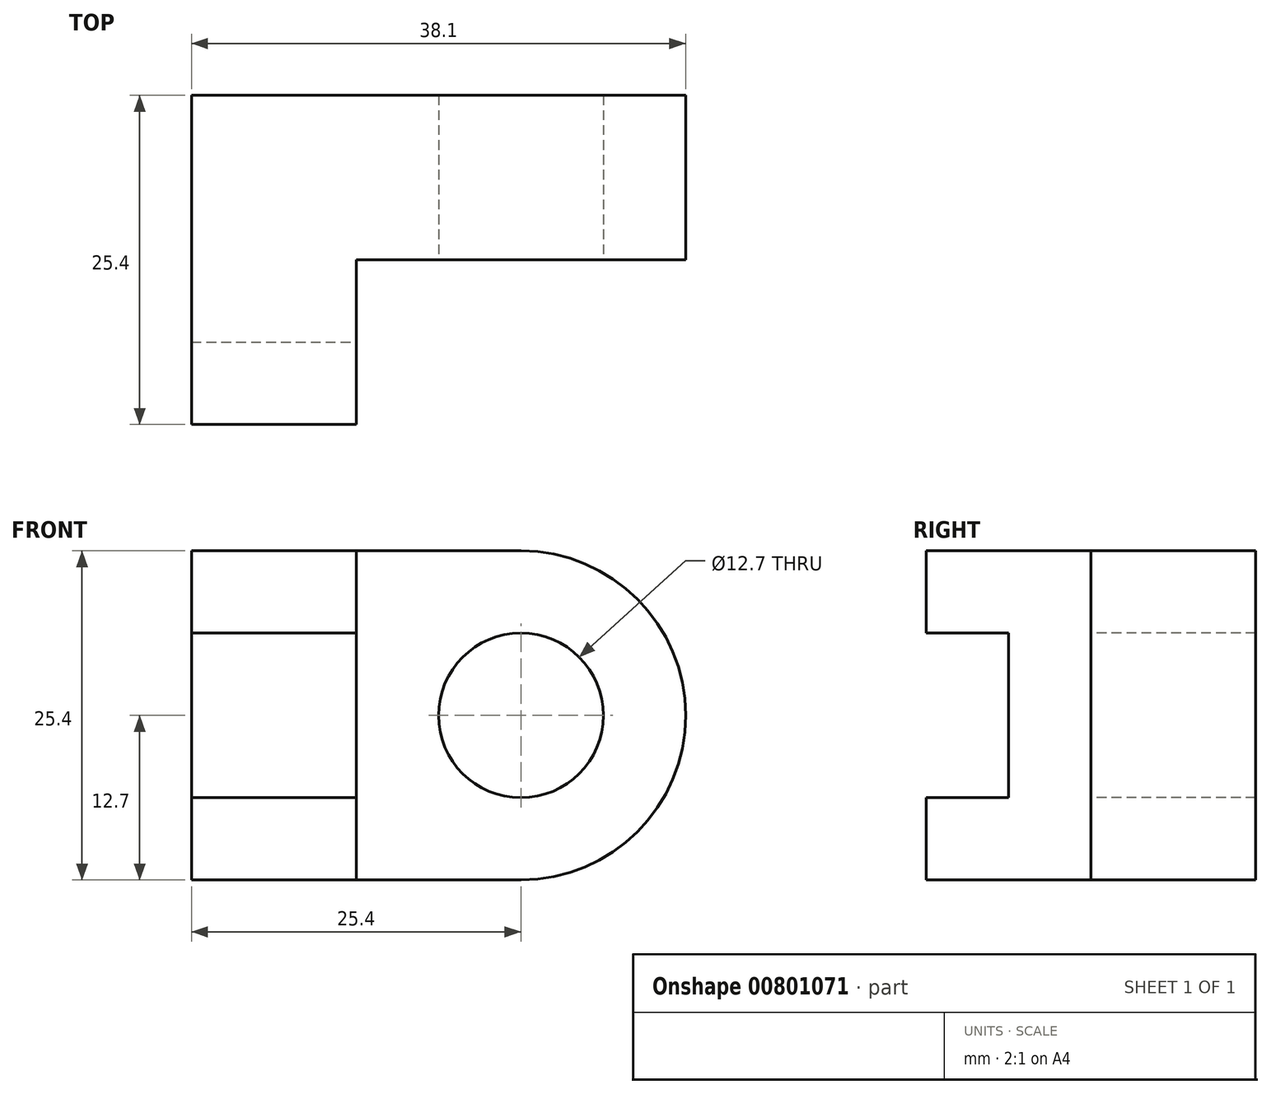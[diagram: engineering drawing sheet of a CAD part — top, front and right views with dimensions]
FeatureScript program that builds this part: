
annotation { "Feature Type Name" : "Feature", "Feature Type Description" : "" }
export const myFeature = defineFeature(function(context is Context, id is Id, definition is map)
    precondition{}
    {
        {
            var Q0;
            Q0=qCreatedBy(makeId("Front.planeOp"),FACE);
            var sketch = newSketch(context, id + "F0", { "sketchPlane" : qUnion([Q0])});
            skLineSegment(sketch, "E0", {"start": v(0, 0) * mm, "end": v(44.45, 0) * mm});
            skLineSegment(sketch, "E1", {"start": v(0, 0) * mm, "end": v(0, 25.4) * mm});
            skLineSegment(sketch, "E2", {"start": v(0, 25.4) * mm, "end": v(44.45, 25.4) * mm});
            skLineSegment(sketch, "E3", {"start": v(44.45, 25.4) * mm, "end": v(44.45, 0) * mm});
            skSolve(sketch);
        }
        {
            var Q0;
            Q0=makeQuery(id+"F0.imprint","IMPRINT",FACE,{"disambiguationData":[TD([[makeQuery(id+"F0.imprint","IMPRINT",EDGE,{"derivedFrom":sQuery(id+"F0.wireOp",EDGE,"E0")}),1.0]])]});
            extrude(context, id + "F1", {"entities" : qUnion([Q0]), "depth" : 25.4 * mm, "offsetDistance" : 25.4 * mm});
        }
        {
            var Q0;
            Q0=makeQuery(id+"F1.opExtrude","CAP_FACE",FACE,{"disambiguationData":[OSD([sQuery(id+"F0.wireOp",EDGE,"E0"),sQuery(id+"F0.wireOp",EDGE,"E1"),sQuery(id+"F0.wireOp",EDGE,"E2"),sQuery(id+"F0.wireOp",EDGE,"E3")])],"isStart":false});
            var sketch = newSketch(context, id + "F2", { "sketchPlane" : qUnion([Q0])});
            skLineSegment(sketch, "E4", {"start": v(0, 25.4) * mm, "end": v(0, 19.05) * mm, "construction": true});
            skLineSegment(sketch, "E5", {"start": v(0, 0) * mm, "end": v(0, 6.35) * mm, "construction": true});
            skLineSegment(sketch, "E6", {"start": v(0, 25.4) * mm, "end": v(12.7, 25.4) * mm, "construction": true});
            skLineSegment(sketch, "E7", {"start": v(12.7, 25.4) * mm, "end": v(12.7, 0) * mm, "construction": true});
            skLineSegment(sketch, "E8", {"start": v(0, 19.05) * mm, "end": v(12.7, 19.05) * mm});
            skLineSegment(sketch, "E9", {"start": v(12.7, 19.05) * mm, "end": v(12.7, 6.35) * mm});
            skLineSegment(sketch, "E10", {"start": v(12.7, 6.35) * mm, "end": v(0, 6.35) * mm});
            skLineSegment(sketch, "E11", {"start": v(0, 6.35) * mm, "end": v(0, 19.05) * mm});
            skSolve(sketch);
        }
        {
            var Q0;
            Q0=makeQuery(id+"F2.imprint","IMPRINT",FACE,{"disambiguationData":[TD([[makeQuery(id+"F2.imprint","IMPRINT",EDGE,{"derivedFrom":sQuery(id+"F2.wireOp",EDGE,"E8")}),-1.0]])]});
            extrude(context, id + "F3", {"entities" : qUnion([Q0]), "operationType" : NewBodyOperationType.REMOVE, "oppositeDirection" : true, "depth" : 6.35 * mm, "offsetDistance" : 25.4 * mm});
        }
        {
            var Q0;
            Q0=makeQuery(id+"F1.opExtrude","SWEPT_FACE",FACE,{"disambiguationData":[OSD([sQuery(id+"F0.wireOp",EDGE,"E2")])]});
            var sketch = newSketch(context, id + "F4", { "sketchPlane" : qUnion([Q0])});
            skLineSegment(sketch, "E12", {"start": v(0, -25.4) * mm, "end": v(12.7, -25.4) * mm, "construction": true});
            skLineSegment(sketch, "E13", {"start": v(12.7, -25.4) * mm, "end": v(12.7, -12.7) * mm, "construction": true});
            skLineSegment(sketch, "E14", {"start": v(12.7, -25.4) * mm, "end": v(12.7, -12.7) * mm});
            skLineSegment(sketch, "E15", {"start": v(12.7, -12.7) * mm, "end": v(44.45, -12.7) * mm});
            skLineSegment(sketch, "E16", {"start": v(44.45, -12.7) * mm, "end": v(44.45, -25.4) * mm});
            skLineSegment(sketch, "E17", {"start": v(44.45, -25.4) * mm, "end": v(12.7, -25.4) * mm});
            skSolve(sketch);
        }
        {
            var Q0;
            Q0=makeQuery(id+"F4.imprint","IMPRINT",FACE,{"disambiguationData":[TD([[makeQuery(id+"F4.imprint","IMPRINT",EDGE,{"derivedFrom":sQuery(id+"F4.wireOp",EDGE,"E14")}),-1.0]])]});
            extrude(context, id + "F5", {"entities" : qUnion([Q0]), "operationType" : NewBodyOperationType.REMOVE, "oppositeDirection" : true, "depth" : 25.4 * mm, "offsetDistance" : 25.4 * mm});
        }
        {
            var Q0;
            Q0=makeQuery(id+"F5.boolean.opBoolean","COPY",FACE,{"derivedFrom":makeQuery(id+"F5.opExtrude","SWEPT_FACE",FACE,{"disambiguationData":[OSD([sQuery(id+"F4.wireOp",EDGE,"E15")])]})});
            var sketch = newSketch(context, id + "F6", { "sketchPlane" : qUnion([Q0])});
            skLineSegment(sketch, "E18", {"start": v(12.7, 25.4) * mm, "end": v(25.4, 25.4) * mm, "construction": true});
            skLineSegment(sketch, "E19", {"start": v(12.7, 0) * mm, "end": v(25.4, 0) * mm, "construction": true});
            skArc(sketch, "E20", {"start": v(25.4, 0) * mm, "mid": v(38.1, 12.7) * mm, "end": v(25.4, 25.4) * mm});
            skSolve(sketch);
        }
        {
            var Q0;
            {var subQ0=sQuery(id+"F6.wireOp",EDGE,"E20");Q0=makeQuery(id+"F6.imprint","IMPRINT",FACE,{"disambiguationData":[TD([[makeQuery(id+"F6.imprint","IMPRINT",EDGE,{"derivedFrom":subQ0}),-1.0]])]});}
            extrude(context, id + "F7", {"entities" : qUnion([Q0]), "operationType" : NewBodyOperationType.REMOVE, "endBound" : BoundingType.UP_TO_NEXT, "oppositeDirection" : true, "depth" : 25.4 * mm, "offsetDistance" : 25.4 * mm});
        }
        {
            var Q0;
            Q0=makeQuery(id+"F5.boolean.opBoolean","COPY",FACE,{"derivedFrom":makeQuery(id+"F5.opExtrude","SWEPT_FACE",FACE,{"disambiguationData":[OSD([sQuery(id+"F4.wireOp",EDGE,"E15")])]})});
            var sketch = newSketch(context, id + "F8", { "sketchPlane" : qUnion([Q0])});
            skLineSegment(sketch, "E21", {"start": v(12.7, 25.4) * mm, "end": v(19.05, 25.4) * mm, "construction": true});
            skLineSegment(sketch, "E22", {"start": v(12.7, 0) * mm, "end": v(19.05, 0) * mm, "construction": true});
            skLineSegment(sketch, "E23", {"start": v(19.05, 25.4) * mm, "end": v(19.05, 0) * mm, "construction": true});
            skLineSegment(sketch, "E24", {"start": v(19.05, 0) * mm, "end": v(25.4, 0) * mm, "construction": true});
            skLineSegment(sketch, "E25", {"start": v(25.4, 0) * mm, "end": v(25.4, 25.4) * mm, "construction": true});
            skCircle(sketch, "E26", {"center": v(25.4, 12.7) * mm, "radius": 6.35 * mm});
            skSolve(sketch);
        }
        {
            var Q0;
            Q0=makeQuery(id+"F8.imprint","IMPRINT",FACE,{"disambiguationData":[TD([[makeQuery(id+"F8.imprint","IMPRINT",EDGE,{"derivedFrom":sQuery(id+"F8.wireOp",EDGE,"E26")}),1.0]])]});
            extrude(context, id + "F9", {"entities" : qUnion([Q0]), "operationType" : NewBodyOperationType.REMOVE, "endBound" : BoundingType.UP_TO_NEXT, "oppositeDirection" : true, "depth" : 25.4 * mm, "offsetDistance" : 25.4 * mm});
        }
    });
